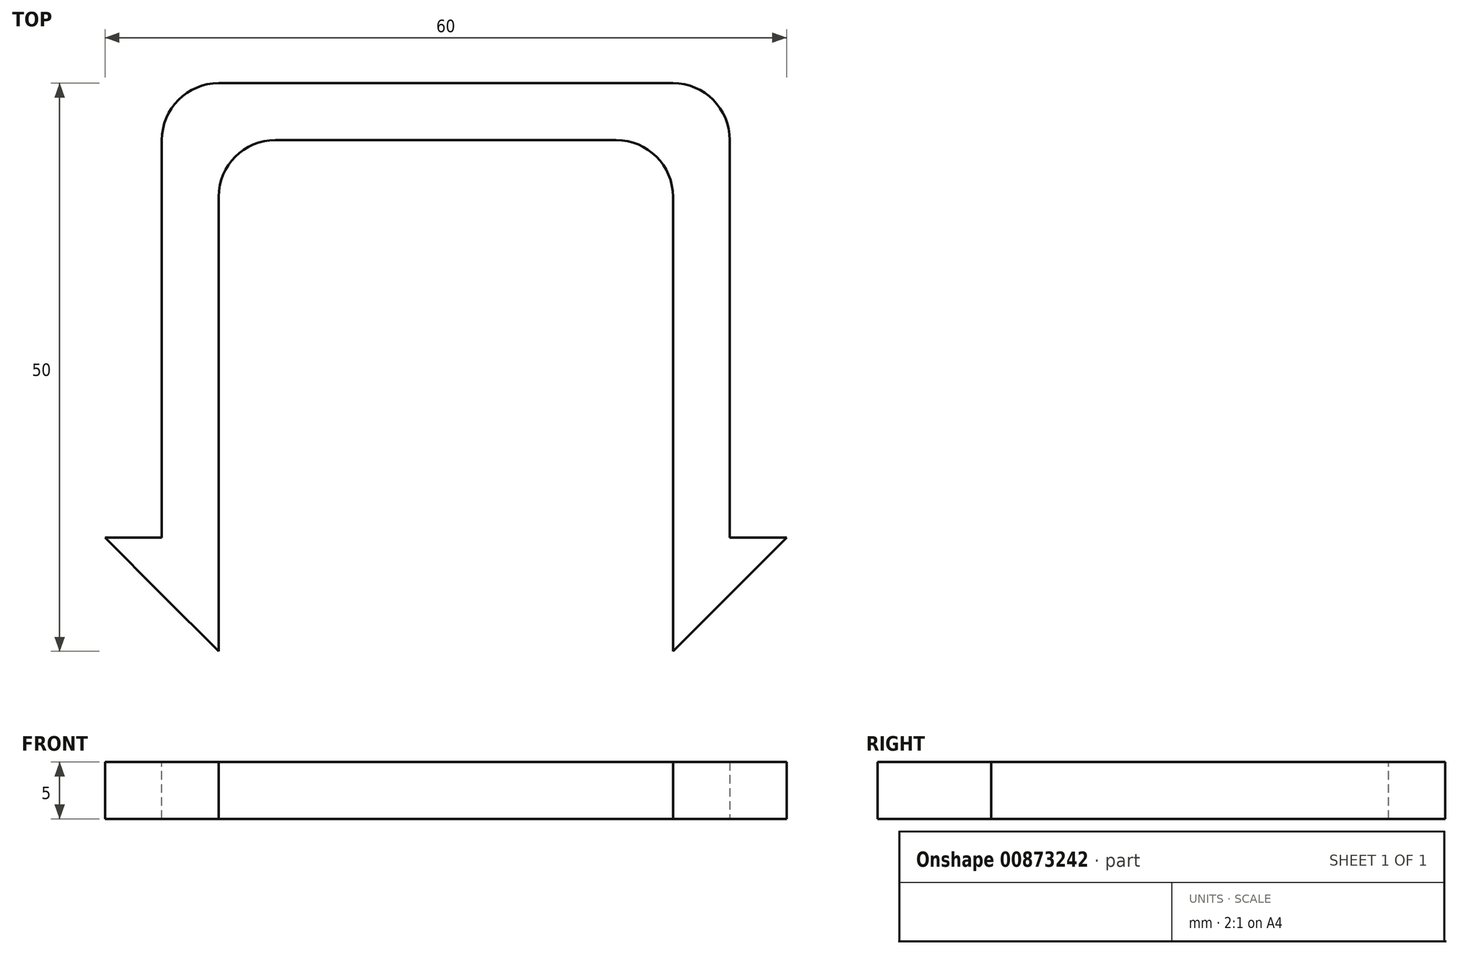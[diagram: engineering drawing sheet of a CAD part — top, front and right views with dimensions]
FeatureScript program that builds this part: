
annotation { "Feature Type Name" : "Feature", "Feature Type Description" : "" }
export const myFeature = defineFeature(function(context is Context, id is Id, definition is map)
    precondition{}
    {
        {
            var Q0;
            Q0=qCreatedBy(makeId("Top.planeOp"),FACE);
            var sketch = newSketch(context, id + "F0", { "sketchPlane" : qUnion([Q0])});
            skLineSegment(sketch, "E0.bottom", {"start": v(25, -25) * mm, "end": v(-25, -25) * mm});
            skLineSegment(sketch, "E0.top", {"start": v(25, 25) * mm, "end": v(-25, 25) * mm});
            skLineSegment(sketch, "E0.left", {"start": v(25, -25) * mm, "end": v(25, 25) * mm});
            skLineSegment(sketch, "E0.right", {"start": v(-25, -25) * mm, "end": v(-25, 25) * mm});
            skPoint(sketch, "E0.middle", {"position": v(0, 0) * mm});
            skSolve(sketch);
        }
        {
            var Q0;
            Q0 = qSketchRegion(id + "F0", true);
            extrude(context, id + "F1", {"entities" : qUnion([Q0]), "depth" : 5 * mm, "offsetDistance" : 25 * mm});
        }
        {
            var Q0;
            Q0=makeQuery(id+"F1.opExtrude","CAP_FACE",FACE,{"disambiguationData":[OSD([sQuery(id+"F0.wireOp",EDGE,"E0.bottom"),sQuery(id+"F0.wireOp",EDGE,"E0.top"),sQuery(id+"F0.wireOp",EDGE,"E0.left"),sQuery(id+"F0.wireOp",EDGE,"E0.right")])],"isStart":false});
            var sketch = newSketch(context, id + "F2", { "sketchPlane" : qUnion([Q0])});
            skPoint(sketch, "E1", {"position": v(-20, -25) * mm});
            skPoint(sketch, "E2", {"position": v(-20, 20) * mm});
            skPoint(sketch, "E3", {"position": v(20, 20) * mm});
            skPoint(sketch, "E4", {"position": v(20, -25) * mm});
            skLineSegment(sketch, "E5", {"start": v(-20, -25) * mm, "end": v(-20, 20) * mm});
            skLineSegment(sketch, "E6", {"start": v(20, 20) * mm, "end": v(20, -25) * mm});
            skLineSegment(sketch, "E7", {"start": v(20, 20) * mm, "end": v(-20, 20) * mm});
            skSolve(sketch);
        }
        {
            var Q0;
            Q0 = qSketchRegion(id + "F2", true);
            var Q1;
            {var subQ0=sQuery(id+"F2.wireOp",EDGE,"E5");Q1=makeQuery(id+"F2.imprint","IMPRINT",FACE,{"disambiguationData":[TD([[makeQuery(id+"F2.imprint","IMPRINT",EDGE,{"derivedFrom":subQ0}),-1.0]])]});}
            extrude(context, id + "F3", {"entities" : qUnion([Q0, Q1]), "operationType" : NewBodyOperationType.REMOVE, "endBound" : BoundingType.THROUGH_ALL, "oppositeDirection" : true, "depth" : 25 * mm, "offsetDistance" : 25 * mm});
        }
        {
            var Q0;
            Q0=makeQuery(id+"F3.boolean.opBoolean","COPY",EDGE,{"derivedFrom":makeQuery(id+"F3.opExtrude","SWEPT_EDGE",EDGE,{"disambiguationData":[OSD([sQuery(id+"F2.wireOp",EDGE,"E5"),sQuery(id+"F2.wireOp",EDGE,"E7")])]})});
            var Q1;
            Q1=makeQuery(id+"F3.boolean.opBoolean","COPY",EDGE,{"derivedFrom":makeQuery(id+"F3.opExtrude","SWEPT_EDGE",EDGE,{"disambiguationData":[OSD([sQuery(id+"F2.wireOp",EDGE,"E6"),sQuery(id+"F2.wireOp",EDGE,"E7")])]})});
            var Q2;
            Q2=makeQuery(id+"F1.opExtrude","SWEPT_EDGE",EDGE,{"disambiguationData":[OSD([sQuery(id+"F0.wireOp",EDGE,"E0.top"),sQuery(id+"F0.wireOp",EDGE,"E0.left")])]});
            var Q3;
            Q3=makeQuery(id+"F1.opExtrude","SWEPT_EDGE",EDGE,{"disambiguationData":[OSD([sQuery(id+"F0.wireOp",EDGE,"E0.top"),sQuery(id+"F0.wireOp",EDGE,"E0.right")])]});
            fillet(context, id + "F4", {"entities" : qUnion([Q0, Q1, Q2, Q3]), "radius" : 5 * mm, "tangentPropagation" : true, "allowEdgeOverflow" : false});
        }
        {
            var Q0;
            Q0=makeQuery(id+"F1.opExtrude","CAP_FACE",FACE,{"disambiguationData":[OSD([sQuery(id+"F0.wireOp",EDGE,"E0.bottom"),sQuery(id+"F0.wireOp",EDGE,"E0.top"),sQuery(id+"F0.wireOp",EDGE,"E0.left"),sQuery(id+"F0.wireOp",EDGE,"E0.right")])],"isStart":false});
            var sketch = newSketch(context, id + "F5", { "sketchPlane" : qUnion([Q0])});
            skPoint(sketch, "E8", {"position": v(-25, -15) * mm});
            skPoint(sketch, "E9", {"position": v(25, -20) * mm});
            skPoint(sketch, "E10", {"position": v(30, -20) * mm});
            skPoint(sketch, "E11", {"position": v(-30, -15) * mm});
            skLineSegment(sketch, "E12", {"start": v(-25, -15) * mm, "end": v(-30, -15) * mm});
            skLineSegment(sketch, "E13", {"start": v(-30, -15) * mm, "end": v(-20, -25) * mm});
            skSolve(sketch);
        }
        {
            var Q0;
            {var subQ0=sQuery(id+"F5.wireOp",EDGE,"E12");Q0=makeQuery(id+"F5.imprint","IMPRINT",FACE,{"disambiguationData":[TD([[makeQuery(id+"F5.imprint","IMPRINT",EDGE,{"derivedFrom":subQ0}),1.0]])]});}
            extrude(context, id + "F6", {"entities" : qUnion([Q0]), "operationType" : NewBodyOperationType.ADD, "oppositeDirection" : true, "depth" : 5 * mm, "offsetDistance" : 25 * mm});
        }
        {
            var Q0;
            {var subQ0=sQuery(id+"F0.wireOp",EDGE,"E0.right");Q0=makeQuery(id+"F6.boolean.opBoolean","MERGE",FACE,{"derivedFrom":[makeQuery(id+"F1.opExtrude","CAP_FACE",FACE,{"disambiguationData":[OSD([sQuery(id+"F0.wireOp",EDGE,"E0.bottom"),sQuery(id+"F0.wireOp",EDGE,"E0.top"),sQuery(id+"F0.wireOp",EDGE,"E0.left"),subQ0])],"isStart":false}),makeQuery(id+"F6.opExtrude","CAP_FACE",FACE,{"disambiguationData":[OSD([subQ0,sQuery(id+"F5.wireOp",EDGE,"E12"),sQuery(id+"F5.wireOp",EDGE,"E13")])],"isStart":true})]});}
            var sketch = newSketch(context, id + "F7", { "sketchPlane" : qUnion([Q0])});
            skLineSegment(sketch, "E14", {"start": v(-30, -15) * mm, "end": v(-20, -25) * mm});
            skSolve(sketch);
        }
        {
            var Q0;
            Q0 = qSketchRegion(id + "F7", true);
            var Q1;
            {var subQ2=sQuery(id+"F0.wireOp",EDGE,"E0.bottom");var subQ4=sQuery(id+"F0.wireOp",EDGE,"E0.right");var subQ5=makeQuery(id+"F1.opExtrude","SWEPT_FACE",FACE,{"disambiguationData":[OSD([subQ4])]});var subQ7=makeQuery(id+"F3.boolean.opBoolean","SPLIT",EDGE,{"disambiguationData":[TD([subQ5])],"derivedFrom":makeQuery(id+"F1.opExtrude","CAP_EDGE",EDGE,{"disambiguationData":[OSD([subQ2])],"isStart":false})});Q1=makeQuery(id+"F7.imprint","IMPRINT",FACE,{"disambiguationData":[TD([[makeQuery(id+"F7.imprint","IMPRINT",EDGE,{"derivedFrom":subQ7}),-1.0]])]});}
            extrude(context, id + "F8", {"entities" : qUnion([Q0, Q1]), "operationType" : NewBodyOperationType.REMOVE, "endBound" : BoundingType.THROUGH_ALL, "oppositeDirection" : true, "depth" : 25 * mm, "offsetDistance" : 25 * mm});
        }
        {
            var Q0;
            Q0=qCreatedBy(makeId("Top.planeOp"),FACE);
            var sketch = newSketch(context, id + "F9", { "sketchPlane" : qUnion([Q0])});
            skPoint(sketch, "E15", {"position": v(30, -15) * mm});
            skPoint(sketch, "E16", {"position": v(25, -25) * mm});
            skLineSegment(sketch, "E17", {"start": v(25, -15) * mm, "end": v(30, -15) * mm});
            skLineSegment(sketch, "E18", {"start": v(30, -15) * mm, "end": v(20, -25) * mm});
            skLineSegment(sketch, "E19", {"start": v(30, -15) * mm, "end": v(30, -25) * mm});
            skLineSegment(sketch, "E20", {"start": v(30, -25) * mm, "end": v(25, -25) * mm});
            skLineSegment(sketch, "E21", {"start": v(25, -20) * mm, "end": v(30, -15) * mm});
            skLineSegment(sketch, "E22", {"start": v(25, -15) * mm, "end": v(25, -25) * mm});
            skSolve(sketch);
        }
        {
            var Q0;
            {var subQ0=sQuery(id+"F9.wireOp",EDGE,"E17");Q0=makeQuery(id+"F9.imprint","IMPRINT",FACE,{"disambiguationData":[TD([[makeQuery(id+"F9.imprint","IMPRINT",EDGE,{"derivedFrom":subQ0}),-1.0]])]});}
            extrude(context, id + "F10", {"entities" : qUnion([Q0]), "operationType" : NewBodyOperationType.ADD, "depth" : 5 * mm, "offsetDistance" : 25 * mm});
        }
        {
            var Q0;
            {var subQ0=sQuery(id+"F0.wireOp",EDGE,"E0.right");Q0=makeQuery(id+"F10.boolean.opBoolean","MERGE",FACE,{"derivedFrom":[makeQuery(id+"F6.boolean.opBoolean","MERGE",FACE,{"derivedFrom":[makeQuery(id+"F1.opExtrude","CAP_FACE",FACE,{"disambiguationData":[OSD([sQuery(id+"F0.wireOp",EDGE,"E0.bottom"),sQuery(id+"F0.wireOp",EDGE,"E0.top"),sQuery(id+"F0.wireOp",EDGE,"E0.left"),subQ0])],"isStart":false}),makeQuery(id+"F6.opExtrude","CAP_FACE",FACE,{"disambiguationData":[OSD([subQ0,sQuery(id+"F5.wireOp",EDGE,"E12"),sQuery(id+"F5.wireOp",EDGE,"E13")])],"isStart":true})]}),makeQuery(id+"F10.opExtrude","CAP_FACE",FACE,{"disambiguationData":[OSD([sQuery(id+"F9.wireOp",EDGE,"E17"),sQuery(id+"F9.wireOp",EDGE,"E21"),sQuery(id+"F9.wireOp",EDGE,"E22")])],"isStart":false})]});}
            var sketch = newSketch(context, id + "F11", { "sketchPlane" : qUnion([Q0])});
            skLineSegment(sketch, "E23", {"start": v(25, -20) * mm, "end": v(20, -25) * mm});
            skLineSegment(sketch, "E24", {"start": v(20, -25) * mm, "end": v(25, -25) * mm});
            skLineSegment(sketch, "E25", {"start": v(25, -25) * mm, "end": v(25, -20) * mm});
            skSolve(sketch);
        }
        {
            var Q0;
            Q0 = qSketchRegion(id + "F11", true);
            extrude(context, id + "F12", {"entities" : qUnion([Q0]), "operationType" : NewBodyOperationType.REMOVE, "endBound" : BoundingType.THROUGH_ALL, "oppositeDirection" : true, "depth" : 25 * mm, "offsetDistance" : 25 * mm});
        }
    });
